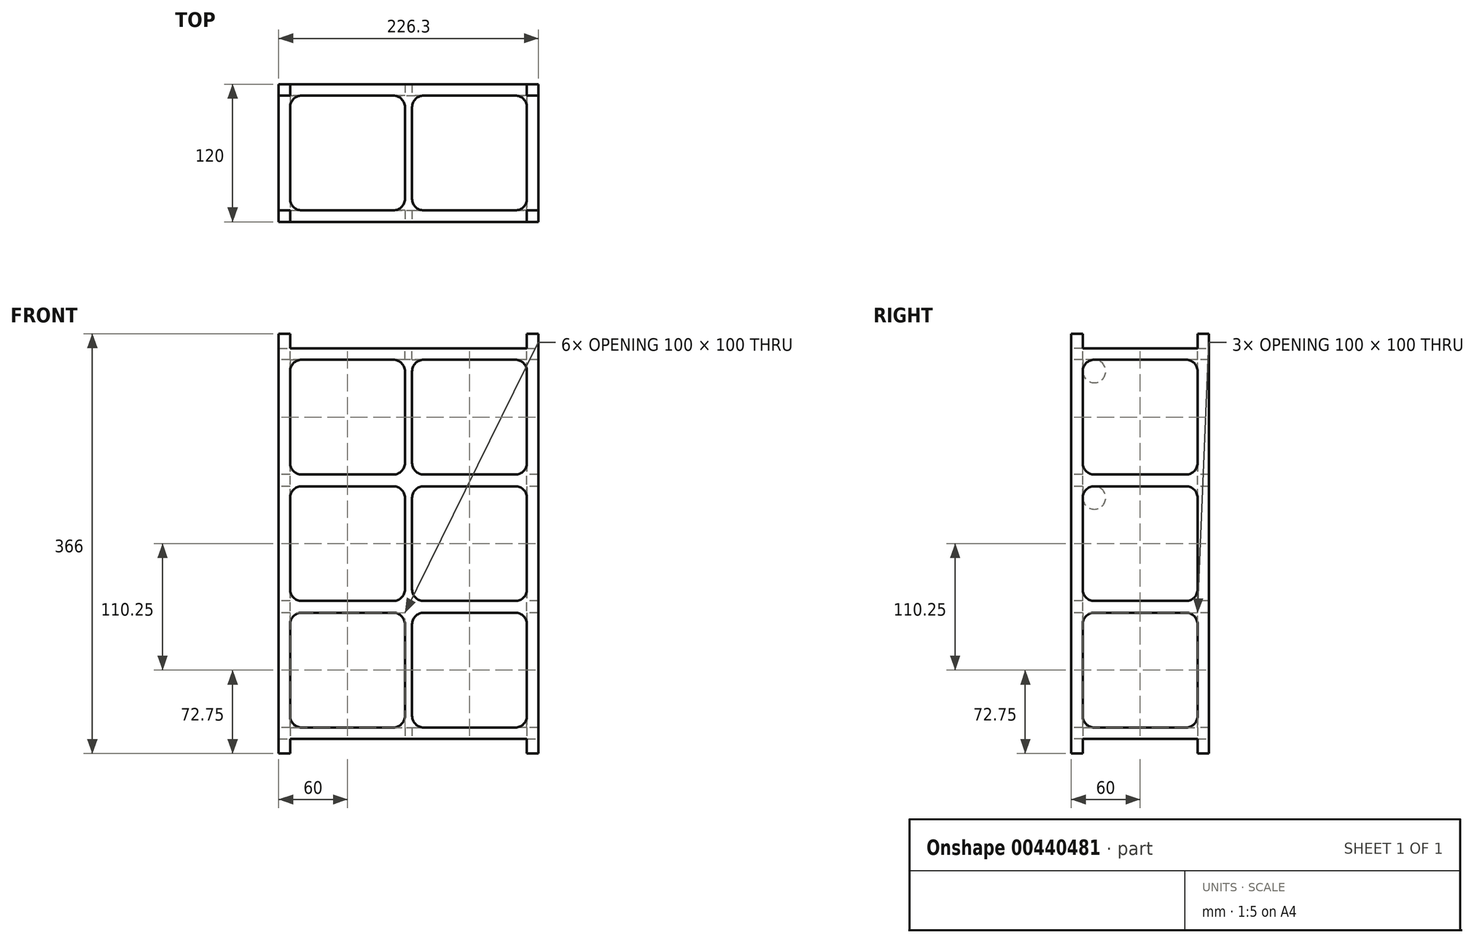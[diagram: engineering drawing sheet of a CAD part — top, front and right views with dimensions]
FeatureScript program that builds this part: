
annotation { "Feature Type Name" : "Feature", "Feature Type Description" : "" }
export const myFeature = defineFeature(function(context is Context, id is Id, definition is map)
    precondition{}
    {
        {
            var Q0;
            Q0=qCreatedBy(makeId("Top.planeOp"),FACE);
            var sketch = newSketch(context, id + "F0", { "sketchPlane" : qUnion([Q0])});
            skLineSegment(sketch, "E0.bottom", {"start": v(113.15, -60) * mm, "end": v(-113.15, -60) * mm});
            skLineSegment(sketch, "E0.top", {"start": v(113.15, 60) * mm, "end": v(-113.15, 60) * mm});
            skLineSegment(sketch, "E0.left", {"start": v(113.15, -60) * mm, "end": v(113.15, 60) * mm});
            skLineSegment(sketch, "E0.right", {"start": v(-113.15, -60) * mm, "end": v(-113.15, 60) * mm});
            skPoint(sketch, "E0.middle", {"position": v(0, 0) * mm});
            skSolve(sketch);
        }
        {
            var Q0;
            Q0 = qSketchRegion(id + "F0", true);
            extrude(context, id + "F1", {"entities" : qUnion([Q0]), "depth" : 366 * mm});
        }
        {
            var Q0;
            Q0=makeQuery(id+"F1.opExtrude","CAP_FACE",FACE,{"disambiguationData":[OSD([sQuery(id+"F0.wireOp",EDGE,"E0.bottom"),sQuery(id+"F0.wireOp",EDGE,"E0.top"),sQuery(id+"F0.wireOp",EDGE,"E0.left"),sQuery(id+"F0.wireOp",EDGE,"E0.right")])],"isStart":false});
            var sketch = newSketch(context, id + "F2", { "sketchPlane" : qUnion([Q0])});
            skLineSegment(sketch, "E1", {"start": v(-113.15, -50) * mm, "end": v(-103.15, -50) * mm});
            skLineSegment(sketch, "E2", {"start": v(-103.15, -50) * mm, "end": v(-103.15, -60) * mm});
            skLineSegment(sketch, "E3", {"start": v(-103.15, -60) * mm, "end": v(103.15, -60) * mm});
            skLineSegment(sketch, "E4", {"start": v(103.15, -60) * mm, "end": v(103.15, -50) * mm});
            skLineSegment(sketch, "E5", {"start": v(103.15, -50) * mm, "end": v(113.15, -50) * mm});
            skLineSegment(sketch, "E6", {"start": v(113.15, -50) * mm, "end": v(113.15, 50) * mm});
            skLineSegment(sketch, "E7", {"start": v(113.15, 50) * mm, "end": v(103.15, 50) * mm});
            skLineSegment(sketch, "E8", {"start": v(103.15, 50) * mm, "end": v(103.15, 60) * mm});
            skLineSegment(sketch, "E9", {"start": v(103.15, 60) * mm, "end": v(-103.15, 60) * mm});
            skLineSegment(sketch, "E10", {"start": v(-103.15, 60) * mm, "end": v(-103.15, 50) * mm});
            skLineSegment(sketch, "E11", {"start": v(-103.15, 50) * mm, "end": v(-113.15, 50) * mm});
            skLineSegment(sketch, "E12", {"start": v(-113.15, 50) * mm, "end": v(-113.15, -50) * mm});
            skSolve(sketch);
        }
        {
            var Q0;
            Q0 = qSketchRegion(id + "F2", true);
            extrude(context, id + "F3", {"entities" : qUnion([Q0]), "operationType" : NewBodyOperationType.REMOVE, "oppositeDirection" : true, "depth" : 12.75 * mm});
        }
        {
            var Q0;
            Q0=makeQuery(id+"F1.opExtrude","CAP_FACE",FACE,{"disambiguationData":[OSD([sQuery(id+"F0.wireOp",EDGE,"E0.bottom"),sQuery(id+"F0.wireOp",EDGE,"E0.top"),sQuery(id+"F0.wireOp",EDGE,"E0.left"),sQuery(id+"F0.wireOp",EDGE,"E0.right")])],"isStart":true});
            var sketch = newSketch(context, id + "F4", { "sketchPlane" : qUnion([Q0])});
            skLineSegment(sketch, "E13", {"start": v(-113.15, -50) * mm, "end": v(-103.15, -50) * mm});
            skLineSegment(sketch, "E14", {"start": v(-103.15, -50) * mm, "end": v(-103.15, -60) * mm});
            skLineSegment(sketch, "E15", {"start": v(-103.15, -60) * mm, "end": v(103.15, -60) * mm});
            skLineSegment(sketch, "E16", {"start": v(103.15, -60) * mm, "end": v(103.15, -50) * mm});
            skLineSegment(sketch, "E17", {"start": v(103.15, -50) * mm, "end": v(113.15, -50) * mm});
            skLineSegment(sketch, "E18", {"start": v(113.15, -50) * mm, "end": v(113.15, 50) * mm});
            skLineSegment(sketch, "E19", {"start": v(113.15, 50) * mm, "end": v(103.15, 50) * mm});
            skLineSegment(sketch, "E20", {"start": v(103.15, 50) * mm, "end": v(103.15, 60) * mm});
            skLineSegment(sketch, "E21", {"start": v(103.15, 60) * mm, "end": v(-103.15, 60) * mm});
            skLineSegment(sketch, "E22", {"start": v(-103.15, 60) * mm, "end": v(-103.15, 50) * mm});
            skLineSegment(sketch, "E23", {"start": v(-103.15, 50) * mm, "end": v(-113.15, 50) * mm});
            skLineSegment(sketch, "E24", {"start": v(-113.15, 50) * mm, "end": v(-113.15, -50) * mm});
            skSolve(sketch);
        }
        {
            var Q0;
            Q0 = qSketchRegion(id + "F4", true);
            extrude(context, id + "F5", {"entities" : qUnion([Q0]), "operationType" : NewBodyOperationType.REMOVE, "oppositeDirection" : true, "depth" : 12.75 * mm});
        }
        {
            var Q0;
            Q0=makeQuery(id+"F3.boolean.opBoolean","COPY",FACE,{"derivedFrom":makeQuery(id+"F3.opExtrude","CAP_FACE",FACE,{"disambiguationData":[OSD([sQuery(id+"F2.wireOp",EDGE,"E1"),sQuery(id+"F2.wireOp",EDGE,"E2"),sQuery(id+"F2.wireOp",EDGE,"E3"),sQuery(id+"F2.wireOp",EDGE,"E4"),sQuery(id+"F2.wireOp",EDGE,"E5"),sQuery(id+"F2.wireOp",EDGE,"E6"),sQuery(id+"F2.wireOp",EDGE,"E7"),sQuery(id+"F2.wireOp",EDGE,"E8"),sQuery(id+"F2.wireOp",EDGE,"E9"),sQuery(id+"F2.wireOp",EDGE,"E10"),sQuery(id+"F2.wireOp",EDGE,"E11"),sQuery(id+"F2.wireOp",EDGE,"E12")])],"isStart":false})});
            var sketch = newSketch(context, id + "F6", { "sketchPlane" : qUnion([Q0])});
            skLineSegment(sketch, "E25.bottom", {"start": v(103.15, 50) * mm, "end": v(-103.15, 50) * mm});
            skLineSegment(sketch, "E25.top", {"start": v(103.15, -50) * mm, "end": v(-103.15, -50) * mm});
            skLineSegment(sketch, "E25.left", {"start": v(103.15, 50) * mm, "end": v(103.15, -50) * mm});
            skLineSegment(sketch, "E25.right", {"start": v(-103.15, 50) * mm, "end": v(-103.15, -50) * mm});
            skSolve(sketch);
        }
        {
            var Q0;
            Q0 = qSketchRegion(id + "F6", true);
            extrude(context, id + "F7", {"entities" : qUnion([Q0]), "operationType" : NewBodyOperationType.REMOVE, "oppositeDirection" : true, "depth" : 340.5 * mm});
        }
        {
            var Q0;
            Q0=makeQuery(id+"F1.opExtrude","SWEPT_FACE",FACE,{"disambiguationData":[OSD([sQuery(id+"F0.wireOp",EDGE,"E0.right")])]});
            var sketch = newSketch(context, id + "F8", { "sketchPlane" : qUnion([Q0])});
            skLineSegment(sketch, "E26.bottom", {"start": v(40, 343.25) * mm, "end": v(-40, 343.25) * mm});
            skLineSegment(sketch, "E26.top", {"start": v(40, 243.25) * mm, "end": v(-40, 243.25) * mm});
            skLineSegment(sketch, "E26.left", {"start": v(50, 333.25) * mm, "end": v(50, 253.25) * mm});
            skLineSegment(sketch, "E26.right", {"start": v(-50, 333.25) * mm, "end": v(-50, 253.25) * mm});
            skLineSegment(sketch, "E27.bottom", {"start": v(40, 233) * mm, "end": v(-40, 233) * mm});
            skLineSegment(sketch, "E27.top", {"start": v(40, 133) * mm, "end": v(-40, 133) * mm});
            skLineSegment(sketch, "E27.left", {"start": v(50, 223) * mm, "end": v(50, 143) * mm});
            skLineSegment(sketch, "E27.right", {"start": v(-50, 223) * mm, "end": v(-50, 143) * mm});
            skLineSegment(sketch, "E28.bottom", {"start": v(40, 22.75) * mm, "end": v(-40, 22.75) * mm});
            skLineSegment(sketch, "E28.top", {"start": v(40, 122.75) * mm, "end": v(-40, 122.75) * mm});
            skLineSegment(sketch, "E28.left", {"start": v(50, 32.75) * mm, "end": v(50, 112.75) * mm});
            skLineSegment(sketch, "E28.right", {"start": v(-50, 32.75) * mm, "end": v(-50, 112.75) * mm});
            skLineSegment(sketch, "E29", {"start": v(-60, 183) * mm, "end": v(60, 183) * mm, "construction": true});
            skPoint(sketch, "E29.startSnap0", {"position": v(-50, 183) * mm});
            skPoint(sketch, "E30.visualSharp", {"position": v(-50, 343.25) * mm});
            skArc(sketch, "E30.filletArc", {"start": v(-40, 343.25) * mm, "mid": v(-47.07, 340.32) * mm, "end": v(-50, 333.25) * mm});
            skPoint(sketch, "E31.visualSharp", {"position": v(50, 343.25) * mm});
            skArc(sketch, "E31.filletArc", {"start": v(50, 333.25) * mm, "mid": v(47.07, 340.32) * mm, "end": v(40, 343.25) * mm});
            skPoint(sketch, "E32.visualSharp", {"position": v(50, 243.25) * mm});
            skArc(sketch, "E32.filletArc", {"start": v(40, 243.25) * mm, "mid": v(47.07, 246.18) * mm, "end": v(50, 253.25) * mm});
            skPoint(sketch, "E33.visualSharp", {"position": v(-50, 243.25) * mm});
            skArc(sketch, "E33.filletArc", {"start": v(-50, 253.25) * mm, "mid": v(-47.07, 246.18) * mm, "end": v(-40, 243.25) * mm});
            skPoint(sketch, "E34.visualSharp", {"position": v(50, 233) * mm});
            skPoint(sketch, "E35.visualSharp", {"position": v(-50, 233) * mm});
            skArc(sketch, "E35.filletArc", {"start": v(-40, 233) * mm, "mid": v(-47.07, 230.07) * mm, "end": v(-50, 223) * mm});
            skPoint(sketch, "E36.visualSharp", {"position": v(-50, 133) * mm});
            skArc(sketch, "E36.filletArc", {"start": v(-50, 143) * mm, "mid": v(-47.07, 135.93) * mm, "end": v(-40, 133) * mm});
            skPoint(sketch, "E37.visualSharp", {"position": v(50, 133) * mm});
            skArc(sketch, "E37.filletArc", {"start": v(40, 133) * mm, "mid": v(47.07, 135.93) * mm, "end": v(50, 143) * mm});
            skPoint(sketch, "E38.visualSharp", {"position": v(-50, 122.75) * mm});
            skArc(sketch, "E38.filletArc", {"start": v(-40, 122.75) * mm, "mid": v(-47.07, 119.82) * mm, "end": v(-50, 112.75) * mm});
            skPoint(sketch, "E39.visualSharp", {"position": v(50, 122.75) * mm});
            skArc(sketch, "E39.filletArc", {"start": v(50, 112.75) * mm, "mid": v(47.07, 119.82) * mm, "end": v(40, 122.75) * mm});
            skPoint(sketch, "E40.visualSharp", {"position": v(-50, 22.75) * mm});
            skArc(sketch, "E40.filletArc", {"start": v(-50, 32.75) * mm, "mid": v(-47.07, 25.68) * mm, "end": v(-40, 22.75) * mm});
            skPoint(sketch, "E41.visualSharp", {"position": v(50, 22.75) * mm});
            skArc(sketch, "E41.filletArc", {"start": v(40, 22.75) * mm, "mid": v(47.07, 25.68) * mm, "end": v(50, 32.75) * mm});
            skArc(sketch, "E42.filletArc", {"start": v(50, 223) * mm, "mid": v(47.07, 230.07) * mm, "end": v(40, 233) * mm});
            skSolve(sketch);
        }
        {
            var Q0;
            Q0 = qSketchRegion(id + "F8", true);
            extrude(context, id + "F9", {"entities" : qUnion([Q0]), "operationType" : NewBodyOperationType.REMOVE, "endBound" : BoundingType.THROUGH_ALL, "oppositeDirection" : true, "depth" : 250 * mm});
        }
        {
            var Q0;
            Q0=makeQuery(id+"F1.opExtrude","SWEPT_FACE",FACE,{"disambiguationData":[OSD([sQuery(id+"F0.wireOp",EDGE,"E0.bottom")])]});
            var sketch = newSketch(context, id + "F10", { "sketchPlane" : qUnion([Q0])});
            skLineSegment(sketch, "E43.bottom", {"start": v(-93.15, 343.25) * mm, "end": v(-13.15, 343.25) * mm});
            skLineSegment(sketch, "E43.top", {"start": v(-93.15, 243.25) * mm, "end": v(-13.15, 243.25) * mm});
            skLineSegment(sketch, "E43.left", {"start": v(-103.15, 333.25) * mm, "end": v(-103.15, 253.25) * mm});
            skLineSegment(sketch, "E43.right", {"start": v(-3.15, 333.25) * mm, "end": v(-3.15, 253.25) * mm});
            skLineSegment(sketch, "E44.bottom", {"start": v(13.15, 243.25) * mm, "end": v(93.15, 243.25) * mm});
            skLineSegment(sketch, "E44.top", {"start": v(13.15, 343.25) * mm, "end": v(93.15, 343.25) * mm});
            skLineSegment(sketch, "E44.left", {"start": v(3.15, 253.25) * mm, "end": v(3.15, 333.25) * mm});
            skLineSegment(sketch, "E44.right", {"start": v(103.15, 253.25) * mm, "end": v(103.15, 333.25) * mm});
            skLineSegment(sketch, "E45.bottom", {"start": v(-93.15, 233) * mm, "end": v(-13.15, 233) * mm});
            skLineSegment(sketch, "E45.top", {"start": v(-93.15, 133) * mm, "end": v(-13.15, 133) * mm});
            skLineSegment(sketch, "E45.left", {"start": v(-103.15, 223) * mm, "end": v(-103.15, 143) * mm});
            skLineSegment(sketch, "E45.right", {"start": v(-3.15, 223) * mm, "end": v(-3.15, 143) * mm});
            skLineSegment(sketch, "E46.bottom", {"start": v(13.15, 233) * mm, "end": v(93.15, 233) * mm});
            skLineSegment(sketch, "E46.top", {"start": v(13.15, 133) * mm, "end": v(93.15, 133) * mm});
            skLineSegment(sketch, "E46.left", {"start": v(3.15, 223) * mm, "end": v(3.15, 143) * mm});
            skLineSegment(sketch, "E46.right", {"start": v(103.15, 223) * mm, "end": v(103.15, 143) * mm});
            skLineSegment(sketch, "E47.bottom", {"start": v(13.15, 122.75) * mm, "end": v(93.15, 122.75) * mm});
            skLineSegment(sketch, "E47.top", {"start": v(13.15, 22.75) * mm, "end": v(93.15, 22.75) * mm});
            skLineSegment(sketch, "E47.left", {"start": v(3.15, 112.75) * mm, "end": v(3.15, 32.75) * mm});
            skLineSegment(sketch, "E47.right", {"start": v(103.15, 112.75) * mm, "end": v(103.15, 32.75) * mm});
            skLineSegment(sketch, "E48.bottom", {"start": v(-13.15, 122.75) * mm, "end": v(-93.15, 122.75) * mm});
            skLineSegment(sketch, "E48.left", {"start": v(-3.15, 112.75) * mm, "end": v(-3.15, 32.75) * mm});
            skLineSegment(sketch, "E49", {"start": v(-103.15, 112.75) * mm, "end": v(-103.15, 32.75) * mm});
            skLineSegment(sketch, "E50", {"start": v(-93.15, 22.75) * mm, "end": v(-13.15, 22.75) * mm});
            skPoint(sketch, "E51.visualSharp", {"position": v(-103.15, 343.25) * mm});
            skArc(sketch, "E51.filletArc", {"start": v(-93.15, 343.25) * mm, "mid": v(-100.22, 340.32) * mm, "end": v(-103.15, 333.25) * mm});
            skPoint(sketch, "E52.visualSharp", {"position": v(-103.15, 243.25) * mm});
            skArc(sketch, "E52.filletArc", {"start": v(-103.15, 253.25) * mm, "mid": v(-100.22, 246.18) * mm, "end": v(-93.15, 243.25) * mm});
            skPoint(sketch, "E53.visualSharp", {"position": v(-3.15, 243.25) * mm});
            skArc(sketch, "E53.filletArc", {"start": v(-13.15, 243.25) * mm, "mid": v(-6.08, 246.18) * mm, "end": v(-3.15, 253.25) * mm});
            skPoint(sketch, "E54.visualSharp", {"position": v(-3.15, 343.25) * mm});
            skArc(sketch, "E54.filletArc", {"start": v(-3.15, 333.25) * mm, "mid": v(-6.08, 340.32) * mm, "end": v(-13.15, 343.25) * mm});
            skPoint(sketch, "E55.visualSharp", {"position": v(3.15, 343.25) * mm});
            skArc(sketch, "E55.filletArc", {"start": v(13.15, 343.25) * mm, "mid": v(6.08, 340.32) * mm, "end": v(3.15, 333.25) * mm});
            skPoint(sketch, "E56.visualSharp", {"position": v(3.15, 243.25) * mm});
            skArc(sketch, "E56.filletArc", {"start": v(3.15, 253.25) * mm, "mid": v(6.08, 246.18) * mm, "end": v(13.15, 243.25) * mm});
            skPoint(sketch, "E57.visualSharp", {"position": v(103.15, 243.25) * mm});
            skArc(sketch, "E57.filletArc", {"start": v(93.15, 243.25) * mm, "mid": v(100.22, 246.18) * mm, "end": v(103.15, 253.25) * mm});
            skPoint(sketch, "E58.visualSharp", {"position": v(103.15, 343.25) * mm});
            skArc(sketch, "E58.filletArc", {"start": v(103.15, 333.25) * mm, "mid": v(100.22, 340.32) * mm, "end": v(93.15, 343.25) * mm});
            skPoint(sketch, "E59.visualSharp", {"position": v(-103.15, 233) * mm});
            skArc(sketch, "E59.filletArc", {"start": v(-93.15, 233) * mm, "mid": v(-100.22, 230.07) * mm, "end": v(-103.15, 223) * mm});
            skPoint(sketch, "E60.visualSharp", {"position": v(-3.15, 233) * mm});
            skArc(sketch, "E60.filletArc", {"start": v(-3.15, 223) * mm, "mid": v(-6.08, 230.07) * mm, "end": v(-13.15, 233) * mm});
            skPoint(sketch, "E61.visualSharp", {"position": v(3.15, 233) * mm});
            skArc(sketch, "E61.filletArc", {"start": v(13.15, 233) * mm, "mid": v(6.08, 230.07) * mm, "end": v(3.15, 223) * mm});
            skPoint(sketch, "E62.visualSharp", {"position": v(103.15, 233) * mm});
            skArc(sketch, "E62.filletArc", {"start": v(103.15, 223) * mm, "mid": v(100.22, 230.07) * mm, "end": v(93.15, 233) * mm});
            skPoint(sketch, "E63.visualSharp", {"position": v(103.15, 133) * mm});
            skArc(sketch, "E63.filletArc", {"start": v(93.15, 133) * mm, "mid": v(100.22, 135.93) * mm, "end": v(103.15, 143) * mm});
            skPoint(sketch, "E64.visualSharp", {"position": v(3.15, 133) * mm});
            skArc(sketch, "E64.filletArc", {"start": v(3.15, 143) * mm, "mid": v(6.08, 135.93) * mm, "end": v(13.15, 133) * mm});
            skPoint(sketch, "E65.visualSharp", {"position": v(-3.15, 133) * mm});
            skArc(sketch, "E65.filletArc", {"start": v(-13.15, 133) * mm, "mid": v(-6.08, 135.93) * mm, "end": v(-3.15, 143) * mm});
            skPoint(sketch, "E66.visualSharp", {"position": v(-103.15, 133) * mm});
            skArc(sketch, "E66.filletArc", {"start": v(-103.15, 143) * mm, "mid": v(-100.22, 135.93) * mm, "end": v(-93.15, 133) * mm});
            skPoint(sketch, "E67.visualSharp", {"position": v(-103.15, 122.75) * mm});
            skArc(sketch, "E67.filletArc", {"start": v(-93.15, 122.75) * mm, "mid": v(-100.22, 119.82) * mm, "end": v(-103.15, 112.75) * mm});
            skPoint(sketch, "E68.visualSharp", {"position": v(-103.15, 22.75) * mm});
            skArc(sketch, "E68.filletArc", {"start": v(-103.15, 32.75) * mm, "mid": v(-100.22, 25.68) * mm, "end": v(-93.15, 22.75) * mm});
            skPoint(sketch, "E69.visualSharp", {"position": v(-3.15, 22.75) * mm});
            skArc(sketch, "E69.filletArc", {"start": v(-13.15, 22.75) * mm, "mid": v(-6.08, 25.68) * mm, "end": v(-3.15, 32.75) * mm});
            skPoint(sketch, "E70.visualSharp", {"position": v(-3.15, 122.75) * mm});
            skArc(sketch, "E70.filletArc", {"start": v(-3.15, 112.75) * mm, "mid": v(-6.08, 119.82) * mm, "end": v(-13.15, 122.75) * mm});
            skPoint(sketch, "E71.visualSharp", {"position": v(3.15, 122.75) * mm});
            skArc(sketch, "E71.filletArc", {"start": v(13.15, 122.75) * mm, "mid": v(6.08, 119.82) * mm, "end": v(3.15, 112.75) * mm});
            skPoint(sketch, "E72.visualSharp", {"position": v(103.15, 122.75) * mm});
            skArc(sketch, "E72.filletArc", {"start": v(103.15, 112.75) * mm, "mid": v(100.22, 119.82) * mm, "end": v(93.15, 122.75) * mm});
            skPoint(sketch, "E73.visualSharp", {"position": v(103.15, 22.75) * mm});
            skArc(sketch, "E73.filletArc", {"start": v(93.15, 22.75) * mm, "mid": v(100.22, 25.68) * mm, "end": v(103.15, 32.75) * mm});
            skPoint(sketch, "E74.visualSharp", {"position": v(3.15, 22.75) * mm});
            skArc(sketch, "E74.filletArc", {"start": v(3.15, 32.75) * mm, "mid": v(6.08, 25.68) * mm, "end": v(13.15, 22.75) * mm});
            skLineSegment(sketch, "E75", {"start": v(-113.15, 183) * mm, "end": v(113.15, 183) * mm, "construction": true});
            skSolve(sketch);
        }
        {
            var Q0;
            Q0 = qSketchRegion(id + "F10", true);
            extrude(context, id + "F11", {"entities" : qUnion([Q0]), "operationType" : NewBodyOperationType.REMOVE, "endBound" : BoundingType.THROUGH_ALL, "oppositeDirection" : true, "depth" : 25 * mm});
        }
        {
            var Q0;
            {var subQ0=sQuery(id+"F2.wireOp",EDGE,"E7");var subQ1=sQuery(id+"F2.wireOp",EDGE,"E8");var subQ2=sQuery(id+"F2.wireOp",EDGE,"E11");var subQ3=sQuery(id+"F2.wireOp",EDGE,"E10");var subQ4=makeQuery(id+"F3.boolean.opBoolean","COPY",FACE,{"derivedFrom":makeQuery(id+"F3.opExtrude","CAP_FACE",FACE,{"disambiguationData":[OSD([sQuery(id+"F2.wireOp",EDGE,"E1"),sQuery(id+"F2.wireOp",EDGE,"E2"),sQuery(id+"F2.wireOp",EDGE,"E3"),sQuery(id+"F2.wireOp",EDGE,"E4"),sQuery(id+"F2.wireOp",EDGE,"E5"),sQuery(id+"F2.wireOp",EDGE,"E6"),subQ0,subQ1,sQuery(id+"F2.wireOp",EDGE,"E9"),subQ3,subQ2,sQuery(id+"F2.wireOp",EDGE,"E12")])],"isStart":false})});Q0=makeQuery(id+"F7.boolean.opBoolean","SPLIT",FACE,{"disambiguationData":[TD([makeQuery(id+"F1.opExtrude","SWEPT_FACE",FACE,{"disambiguationData":[OSD([sQuery(id+"F0.wireOp",EDGE,"E0.top")])]})])],"derivedFrom":subQ4});}
            var sketch = newSketch(context, id + "F12", { "sketchPlane" : qUnion([Q0])});
            skLineSegment(sketch, "E76", {"start": v(-103.15, 50) * mm, "end": v(-103.15, 40) * mm});
            skLineSegment(sketch, "E77", {"start": v(-103.15, 50) * mm, "end": v(-93.15, 50) * mm});
            skArc(sketch, "E78", {"start": v(-93.15, 50) * mm, "mid": v(-100.22, 47.07) * mm, "end": v(-103.15, 40) * mm});
            skLineSegment(sketch, "E79", {"start": v(-103.15, -40) * mm, "end": v(-103.15, -50) * mm});
            skLineSegment(sketch, "E80", {"start": v(-103.15, -50) * mm, "end": v(-93.15, -50) * mm});
            skArc(sketch, "E81", {"start": v(-93.15, -50) * mm, "mid": v(-100.22, -47.07) * mm, "end": v(-103.15, -40) * mm});
            skLineSegment(sketch, "E82", {"start": v(103.15, 50) * mm, "end": v(93.15, 50) * mm});
            skLineSegment(sketch, "E83", {"start": v(103.15, 50) * mm, "end": v(103.15, 40) * mm});
            skArc(sketch, "E84", {"start": v(103.15, 40) * mm, "mid": v(100.22, 47.07) * mm, "end": v(93.15, 50) * mm});
            skLineSegment(sketch, "E85", {"start": v(103.15, -40) * mm, "end": v(103.15, -50) * mm});
            skLineSegment(sketch, "E86", {"start": v(103.15, -50) * mm, "end": v(93.15, -50) * mm});
            skArc(sketch, "E87", {"start": v(103.15, -40) * mm, "mid": v(100.22, -47.07) * mm, "end": v(93.15, -50) * mm});
            skLineSegment(sketch, "E88.left", {"start": v(-3.15, 40) * mm, "end": v(-3.15, -40) * mm});
            skLineSegment(sketch, "E88.right", {"start": v(3.15, 40) * mm, "end": v(3.15, -40) * mm});
            skArc(sketch, "E89", {"start": v(-13.15, 50) * mm, "mid": v(-6.08, 47.07) * mm, "end": v(-3.15, 40) * mm});
            skArc(sketch, "E90", {"start": v(-13.15, -50) * mm, "mid": v(-6.08, -47.07) * mm, "end": v(-3.15, -40) * mm});
            skArc(sketch, "E91", {"start": v(13.15, 50) * mm, "mid": v(6.08, 47.07) * mm, "end": v(3.15, 40) * mm});
            skArc(sketch, "E92", {"start": v(13.15, -50) * mm, "mid": v(6.08, -47.07) * mm, "end": v(3.15, -40) * mm});
            skLineSegment(sketch, "E93", {"start": v(-13.15, 50) * mm, "end": v(13.15, 50) * mm});
            skLineSegment(sketch, "E94", {"start": v(-13.15, -50) * mm, "end": v(13.15, -50) * mm});
            skSolve(sketch);
        }
        {
            var Q0;
            Q0 = qSketchRegion(id + "F12", true);
            extrude(context, id + "F13", {"entities" : qUnion([Q0]), "operationType" : NewBodyOperationType.ADD, "oppositeDirection" : true, "depth" : 10 * mm});
        }
        {
            var Q0;
            {var subQ0=sQuery(id+"F4.wireOp",EDGE,"E23");var subQ1=sQuery(id+"F4.wireOp",EDGE,"E22");var subQ2=sQuery(id+"F4.wireOp",EDGE,"E14");var subQ3=sQuery(id+"F4.wireOp",EDGE,"E13");var subQ4=makeQuery(id+"F5.boolean.opBoolean","COPY",FACE,{"derivedFrom":makeQuery(id+"F5.opExtrude","CAP_FACE",FACE,{"disambiguationData":[OSD([subQ3,subQ2,sQuery(id+"F4.wireOp",EDGE,"E15"),sQuery(id+"F4.wireOp",EDGE,"E16"),sQuery(id+"F4.wireOp",EDGE,"E17"),sQuery(id+"F4.wireOp",EDGE,"E18"),sQuery(id+"F4.wireOp",EDGE,"E19"),sQuery(id+"F4.wireOp",EDGE,"E20"),sQuery(id+"F4.wireOp",EDGE,"E21"),subQ1,subQ0,sQuery(id+"F4.wireOp",EDGE,"E24")])],"isStart":false})});Q0=makeQuery(id+"F7.boolean.opBoolean","SPLIT",FACE,{"disambiguationData":[TD([makeQuery(id+"F1.opExtrude","SWEPT_FACE",FACE,{"disambiguationData":[OSD([sQuery(id+"F0.wireOp",EDGE,"E0.right")])]})])],"derivedFrom":subQ4});}
            var sketch = newSketch(context, id + "F14", { "sketchPlane" : qUnion([Q0])});
            skLineSegment(sketch, "E95", {"start": v(-103.15, 50) * mm, "end": v(-93.15, 50) * mm});
            skLineSegment(sketch, "E96", {"start": v(-103.15, 50) * mm, "end": v(-103.15, 40) * mm});
            skArc(sketch, "E97", {"start": v(-93.15, 50) * mm, "mid": v(-100.22, 47.07) * mm, "end": v(-103.15, 40) * mm});
            skLineSegment(sketch, "E98", {"start": v(-103.15, -50) * mm, "end": v(-103.15, -40) * mm});
            skLineSegment(sketch, "E99", {"start": v(-103.15, -50) * mm, "end": v(-93.15, -50) * mm});
            skArc(sketch, "E100", {"start": v(-93.15, -50) * mm, "mid": v(-100.22, -47.07) * mm, "end": v(-103.15, -40) * mm});
            skLineSegment(sketch, "E101", {"start": v(93.15, 50) * mm, "end": v(103.15, 50) * mm});
            skLineSegment(sketch, "E102", {"start": v(103.15, 50) * mm, "end": v(103.15, 40) * mm});
            skArc(sketch, "E103", {"start": v(93.15, 50) * mm, "mid": v(100.22, 47.07) * mm, "end": v(103.15, 40) * mm});
            skLineSegment(sketch, "E104", {"start": v(103.15, -40) * mm, "end": v(103.15, -50) * mm});
            skLineSegment(sketch, "E105", {"start": v(103.15, -50) * mm, "end": v(93.15, -50) * mm});
            skArc(sketch, "E106", {"start": v(103.15, -40) * mm, "mid": v(100.22, -47.07) * mm, "end": v(93.15, -50) * mm});
            skLineSegment(sketch, "E107", {"start": v(-3.15, 40) * mm, "end": v(-3.15, -40) * mm});
            skLineSegment(sketch, "E108", {"start": v(3.15, 40) * mm, "end": v(3.15, -40) * mm});
            skArc(sketch, "E109", {"start": v(-3.15, 40) * mm, "mid": v(-6.08, 47.07) * mm, "end": v(-13.15, 50) * mm});
            skArc(sketch, "E110", {"start": v(3.15, 40) * mm, "mid": v(6.08, 47.07) * mm, "end": v(13.15, 50) * mm});
            skArc(sketch, "E111", {"start": v(3.15, -40) * mm, "mid": v(6.08, -47.07) * mm, "end": v(13.15, -50) * mm});
            skArc(sketch, "E112", {"start": v(-3.15, -40) * mm, "mid": v(-6.08, -47.07) * mm, "end": v(-13.15, -50) * mm});
            skLineSegment(sketch, "E113", {"start": v(-13.15, -50) * mm, "end": v(13.15, -50) * mm});
            skLineSegment(sketch, "E114", {"start": v(-13.15, 50) * mm, "end": v(13.15, 50) * mm});
            skSolve(sketch);
        }
        {
            var Q0;
            Q0 = qSketchRegion(id + "F14", true);
            extrude(context, id + "F15", {"entities" : qUnion([Q0]), "operationType" : NewBodyOperationType.ADD, "oppositeDirection" : true, "depth" : 10 * mm});
        }
    });
